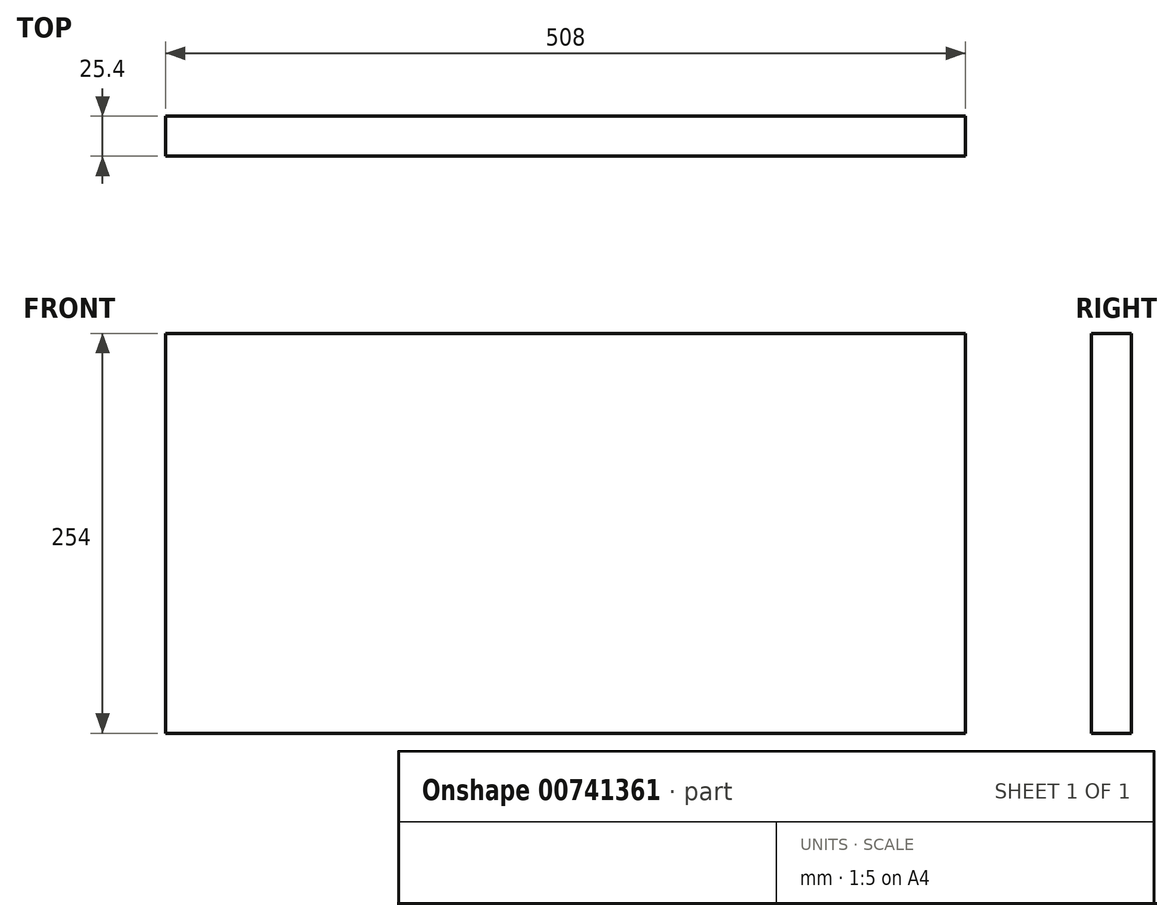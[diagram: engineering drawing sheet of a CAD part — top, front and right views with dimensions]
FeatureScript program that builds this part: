
annotation { "Feature Type Name" : "Feature", "Feature Type Description" : "" }
export const myFeature = defineFeature(function(context is Context, id is Id, definition is map)
    precondition{}
    {
        {
            var Q0;
            Q0=qCreatedBy(makeId("Front.planeOp"),FACE);
            var sketch = newSketch(context, id + "F0", { "sketchPlane" : qUnion([Q0])});
            skLineSegment(sketch, "E0.bottom", {"start": v(-254, 127) * mm, "end": v(254, 127) * mm});
            skLineSegment(sketch, "E0.top", {"start": v(-254, -127) * mm, "end": v(254, -127) * mm});
            skLineSegment(sketch, "E0.left", {"start": v(-254, 127) * mm, "end": v(-254, -127) * mm});
            skLineSegment(sketch, "E0.right", {"start": v(254, 127) * mm, "end": v(254, -127) * mm});
            skPoint(sketch, "E0.middle", {"position": v(0, 0) * mm});
            skSolve(sketch);
        }
        {
            var Q0;
            Q0=makeQuery(id+"F0.imprint","IMPRINT",FACE,{"disambiguationData":[TD([[makeQuery(id+"F0.imprint","IMPRINT",EDGE,{"derivedFrom":sQuery(id+"F0.wireOp",EDGE,"E0.bottom")}),-1.0]])]});
            extrude(context, id + "F1", {"entities" : qUnion([Q0]), "depth" : 25.4 * mm, "offsetDistance" : 25.4 * mm});
        }
    });
